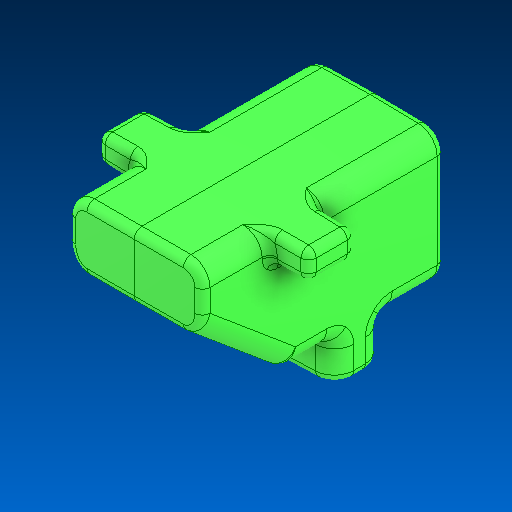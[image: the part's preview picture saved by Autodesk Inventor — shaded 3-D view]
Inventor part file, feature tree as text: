
AUTODESK INVENTOR PART (.ipt)
format: ipt  version: 2022.2 (Build 262287000, 287)  size: 361,472 bytes
history: native  units: in
note: dims shown in document units (in); Inventor stores cm internally (conversion verified against a paired STEP export)
features: fillet x1
ambient origin geometry x8: Origin, YZ Plane, XZ Plane, XY Plane, X Axis, Y Axis, Z Axis, Center Point
bodies: Solid1 (feature_tree)
feature tree (1):
  fillet  "Fillet5"  [1 undecoded]
note: 1 required parameter value undecoded (feature->parameter linkage not recoverable at this tier; creation-order binding heuristic only, values carry confidence <= 0.55)
